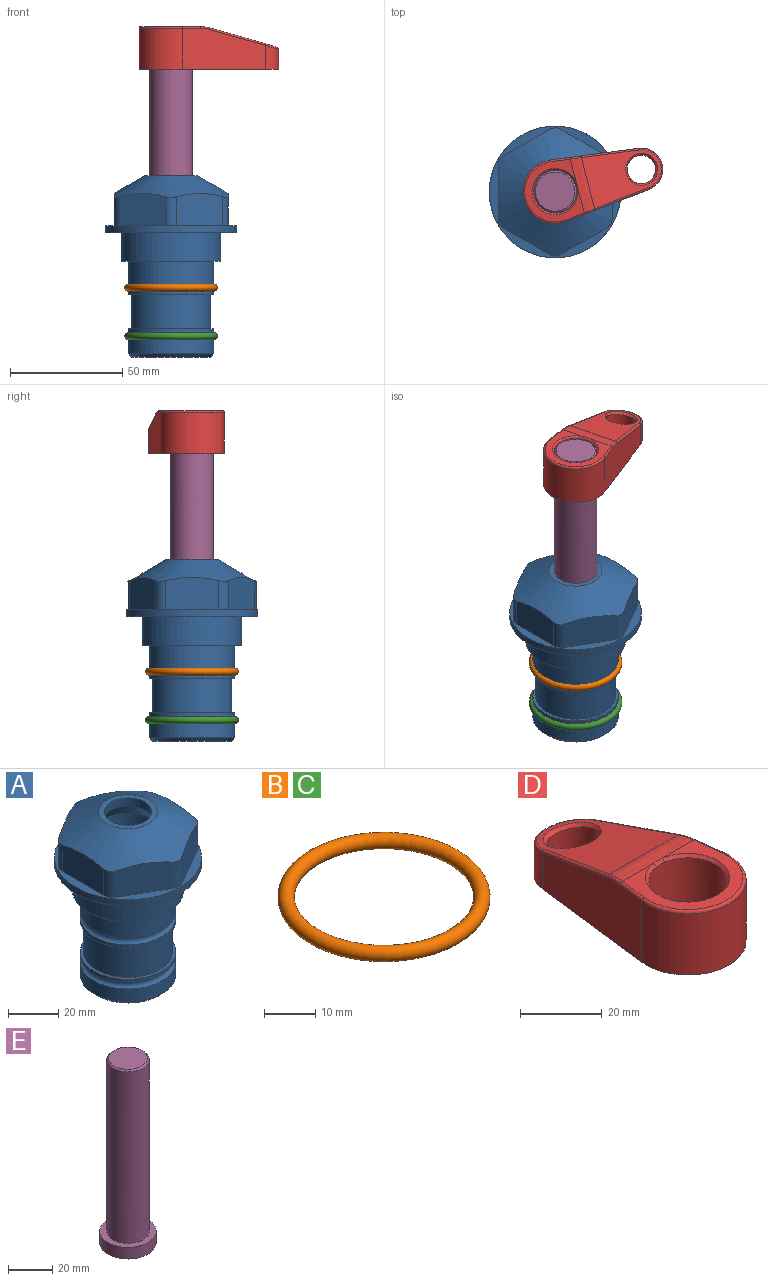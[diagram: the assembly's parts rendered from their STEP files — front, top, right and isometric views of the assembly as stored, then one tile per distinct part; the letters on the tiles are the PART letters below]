
ASSEMBLY  parts=5 mates=4
PART A: 36 faces, bbox 58.7x58.7x81 mm
  f0: cylinder r=17.78mm len=35.56mm, axis (0,0,1), area 1670.8mm2, adj f23,f24,f31
  f1: cylinder r=19.05mm len=38.1mm, axis (0,0,1), area 1191.9mm2, adj f26,f27,f30
  f2: plane 58.66x58.66mm, normal (0,0,-1), area 1150.6mm2, adj f3,f28
  f3: cylinder r=29.33mm len=58.66mm, axis (0,0,-1), area 585.1mm2, adj f2,f4
  f4: plane 58.66x58.66mm, normal (0,0,1), area 475.9mm2, adj f3,f5,f6,f7,f8,f9,f10,f11
  f5: plane 20.32x14.34mm, normal (-0.5,0.87,0), area 324.4mm2, adj f4,f15,f16,f17
  f6: plane 20.32x14.34mm, normal (0.5,0.87,0), area 324.4mm2, adj f4,f14,f15,f17
  f7: plane 23.48x14.34mm, normal (1,0,0), area 324.4mm2, adj f4,f13,f14,f17
  f8: plane 20.32x14.34mm, normal (0.5,-0.87,0), area 324.4mm2, adj f4,f12,f13,f17
  f9: plane 20.32x14.34mm, normal (-0.5,-0.87,0), area 324.4mm2, adj f4,f11,f12,f17
  f10: plane 23.48x14.34mm, normal (-1,0,0), area 324.4mm2, adj f4,f11,f16,f17
  f11: cylinder r=5.08mm len=12.85mm, axis (0,0,-1), area 67.2mm2, adj f4,f9,f10,f17
  f12: cylinder r=5.08mm len=12.85mm, axis (0,0,-1), area 67.2mm2, adj f4,f8,f9,f17
  f13: cylinder r=5.08mm len=12.85mm, axis (0,0,-1), area 67.2mm2, adj f4,f7,f8,f17
  f14: cylinder r=5.08mm len=12.85mm, axis (0,0,-1), area 67.2mm2, adj f4,f6,f7,f17
  f15: cylinder r=5.08mm len=12.85mm, axis (0,0,-1), area 67.2mm2, adj f4,f5,f6,f17
  f16: cylinder r=5.08mm len=12.85mm, axis (0,0,-1), area 67.2mm2, adj f4,f5,f10,f17
  f17: cone r=11.73mm half-angle=60deg, axis (0,0,-1), area 2071.8mm2, adj f5,f6,f7,f8,f9,f10,f11,f12
  f18: plane 23.46x23.46mm, normal (0,0,1), area 147.4mm2, adj f17,f35
  f19: plane 34.93x34.93mm, normal (0,0,-1), area 958mm2, adj f29
  f20: cylinder r=19.05mm len=38.1mm, axis (0,0,1), area 760.1mm2, adj f21,f29
  f21: torus R=19.05mm, axis (0,0,1), area 565.3mm2, adj f20,f22
  f22: cylinder r=19.05mm len=38.1mm, axis (0,0,1), area 190mm2, adj f21,f23
  f23: plane 38.1x38.1mm, normal (0,0,1), area 146.9mm2, adj f0,f22
  f24: plane 38.1x38.1mm, normal (0,0,-1), area 146.9mm2, adj f0,f25
  f25: cylinder r=19.05mm len=38.1mm, axis (0,0,1), area 190mm2, adj f24,f26
  f26: torus R=19.05mm, axis (0,0,1), area 565.3mm2, adj f1,f25
  f27: plane 44.45x44.45mm, normal (0,0,-1), area 411.7mm2, adj f1,f28
  f28: cylinder r=22.23mm len=44.45mm, axis (0,0,1), area 1773.5mm2, adj f2,f27
  f29: cone r=19.05mm half-angle=45deg, axis (0,0,1), area 257.5mm2, adj f19,f20
  f30: cylinder r=3.17mm len=6.75mm, axis (-1,0,0), area 128mm2, adj f1,f33
  f31: cylinder r=3.17mm len=6.35mm, axis (-1,0,0), area 102.5mm2, adj f0,f33
  f32: plane 25.4x25.4mm, normal (0,0,1), area 506.7mm2, adj f33
  f33: cylinder r=12.7mm len=66.42mm, axis (0,0,-1), area 5236.2mm2, adj f30,f31,f32,f34
  f34: cone r=9.53mm half-angle=30deg, axis (0,0,-1), area 443.4mm2, adj f33,f35
  f35: cylinder r=9.53mm len=19.05mm, axis (0,0,-1), area 240.9mm2, adj f18,f34
PART B: 1 faces, bbox 44.7x44.7x3.2 mm
  f0: torus R=19.05mm, axis (0,0,1), area 1193.9mm2
PART C: same geometry as B
PART D: 31 faces, bbox 31.7x65.5x19.8 mm
  f0: plane 39.12x18.26mm, normal (0.99,0.12,0), area 612.2mm2, adj f1,f4,f7,f11,f13,f15
  f1: cylinder r=9.53mm len=18.91mm, axis (0,0,-1), area 296.1mm2, adj f0,f2,f7,f17
  f2: plane 39.12x18.26mm, normal (-0.99,0.12,0), area 612.2mm2, adj f1,f4,f7,f12,f14,f16
  f3: cylinder r=6.35mm len=12.7mm, axis (0,0,-1), area 362.4mm2, adj f7,f18
  f4: cylinder r=14.29mm len=28.58mm, axis (0,0,-1), area 882.2mm2, adj f0,f2,f7,f10
  f5: cylinder r=9.53mm len=19.05mm, axis (0,0,-1), area 1092.6mm2, adj f7,f19,f20
  f6: plane 26.99x23.69mm, normal (0,0,1), area 216.2mm2, adj f9,f10,f11,f12,f19
  f7: plane 63.5x28.58mm, normal (0,0,-1), area 661.8mm2, adj f0,f1,f2,f3,f4,f5,f22,f23
  f8: plane 33.52x23.6mm, normal (0,0.26,0.97), area 486mm2, adj f9,f15,f16,f17,f18
  f9: cylinder r=19.05mm len=24.72mm, axis (1,0,0), area 120.4mm2, adj f6,f8,f13,f14,f20
  f10: torus R=13.49mm, axis (0,0,1), area 59mm2, adj f4,f6,f11,f12
  f11: cylinder r=0.79mm len=8.67mm, axis (0.12,-0.99,0), area 10.8mm2, adj f0,f6,f10,f13
  f12: cylinder r=0.79mm len=8.67mm, axis (0.12,0.99,0), area 10.8mm2, adj f2,f6,f10,f14
  f13: bspline ~4.95x1.42mm, area 6.1mm2, adj f0,f9,f11,f15
  f14: bspline ~4.95x1.42mm, area 6.1mm2, adj f2,f9,f12,f16
  f15: cylinder r=0.79mm len=25.95mm, axis (0.12,-0.96,0.26), area 32.9mm2, adj f0,f8,f13,f17
  f16: cylinder r=0.79mm len=25.95mm, axis (0.12,0.96,-0.26), area 32.9mm2, adj f2,f8,f14,f17
  f17: bspline ~18.91x8.38mm, area 30mm2, adj f1,f8,f15,f16
  f18: bspline ~14.29x14.29mm, area 48.3mm2, adj f3,f8
  f19: cone r=9.53mm half-angle=45deg, axis (0,0,1), area 66.5mm2, adj f5,f6,f20
  f20: bspline ~3.22x0.96mm, area 3.5mm2, adj f5,f9,f19
  f21: plane 2.75x2.72mm, normal (0,0,-1), area 2.9mm2, adj f23,f25,f28
  f22: plane 23.05x15.88mm, normal (-0.99,-0.12,0), area 323.6mm2, adj f7,f25,f26,f27,f28,f29
  f23: plane 23.05x15.88mm, normal (0.99,-0.12,0), area 323.6mm2, adj f7,f21,f25,f27,f28,f30
  f24: cylinder r=9.53mm len=10.69mm, axis (0,0,-1), area 114.7mm2, adj f7,f27,f29,f30
  f25: cylinder r=12.7mm len=20.59mm, axis (0,0,-1), area 381.1mm2, adj f7,f21,f22,f23,f26,f28
  f26: plane 2.75x2.72mm, normal (0,0,-1), area 2.9mm2, adj f22,f25,f28
  f27: plane 19.72x18.37mm, normal (0,-0.26,-0.97), area 291.8mm2, adj f22,f23,f24,f28,f29,f30
  f28: cylinder r=15.88mm len=19.92mm, axis (1,0,0), area 54.8mm2, adj f21,f22,f23,f25,f26,f27
  f29: cylinder r=1.59mm len=11mm, axis (0,0,-1), area 34.7mm2, adj f7,f22,f24,f27
  f30: cylinder r=1.59mm len=11mm, axis (0,0,-1), area 34.7mm2, adj f7,f23,f24,f27
PART E: 6 faces, bbox 25.4x25.4x101.6 mm
  f0: plane 17.46x17.46mm, normal (0,0,1), area 239.5mm2, adj f5
  f1: plane 25.4x25.4mm, normal (0,0,-1), area 506.7mm2, adj f2
  f2: cylinder r=12.7mm len=25.4mm, axis (0,0,1), area 506.7mm2, adj f1,f3
  f3: plane 25.4x25.4mm, normal (0,0,1), area 221.7mm2, adj f2,f4
  f4: cylinder r=9.53mm len=94.46mm, axis (0,0,1), area 5653mm2, adj f3,f5
  f5: cone r=8.73mm half-angle=45deg, axis (0,0,-1), area 64.4mm2, adj f0,f4
PLACE A at identity fixed
PLACE B at identity
PLACE C t=(0,0,-21.59)mm
PLACE D rot(axis=(0,0,-1),75.5deg) t=(0,0,28.35)mm
PLACE E rot(axis=(0,0,-1),75.5deg) t=(0,0,27.55)mm
MATE fastened B.f0 <-> A.f0  axis (0,0,1) through (0,0,-24.51)mm
MATE cylindrical E.f2 <-> A.f0  axis (0,0,-1) through (0,0,-10.55)mm
MATE fastened C.f0 <-> A.f0  axis (0,0,1) through (0,0,-46.1)mm
MATE fastened E.f2 <-> D.f4  axis (0,0,1) through (0,0,91.05)mm
